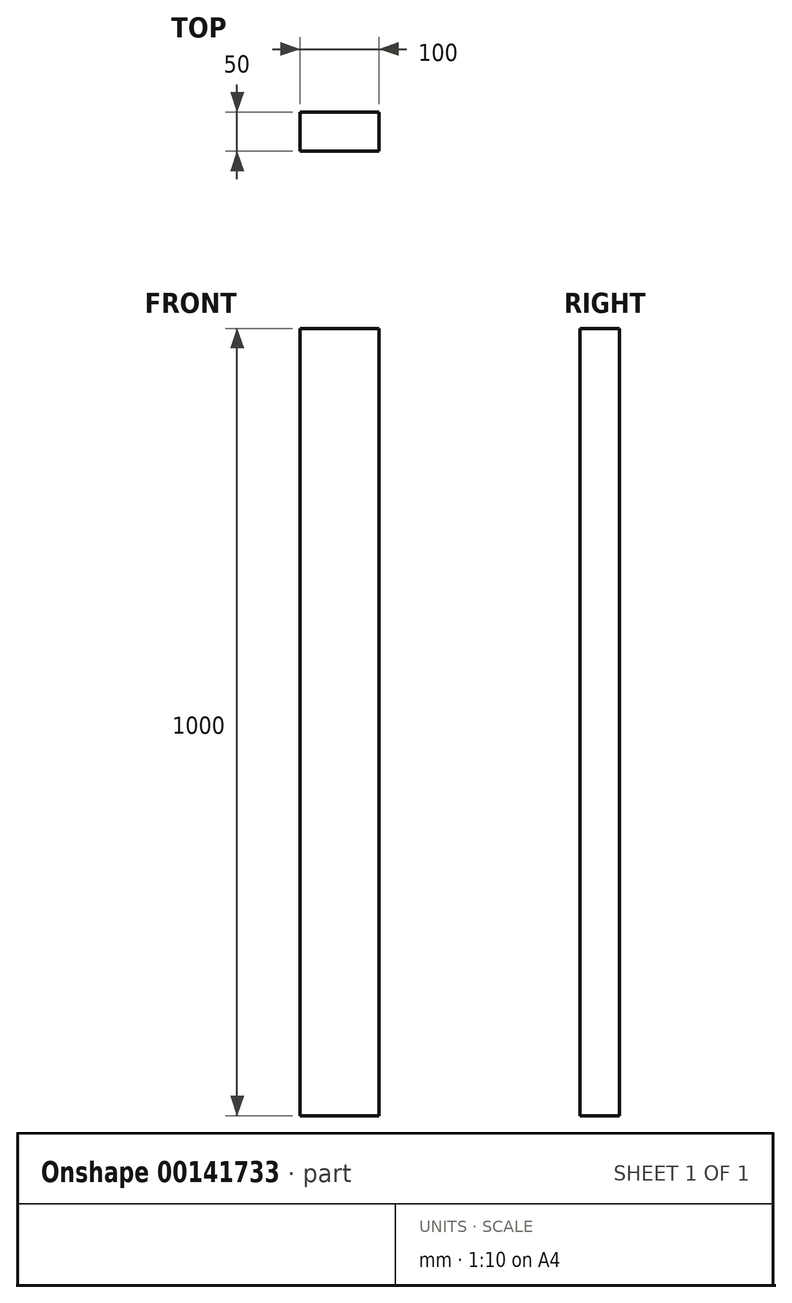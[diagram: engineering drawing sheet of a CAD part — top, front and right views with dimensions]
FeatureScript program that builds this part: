
annotation { "Feature Type Name" : "Feature", "Feature Type Description" : "" }
export const myFeature = defineFeature(function(context is Context, id is Id, definition is map)
    precondition{}
    {
        {
            var Q0;
            Q0=qCreatedBy(makeId("Top.planeOp"),FACE);
            var sketch = newSketch(context, id + "F0", { "sketchPlane" : qUnion([Q0])});
            skLineSegment(sketch, "E0.bottom", {"start": v(50, 25) * mm, "end": v(-50, 25) * mm});
            skLineSegment(sketch, "E0.top", {"start": v(50, -25) * mm, "end": v(-50, -25) * mm});
            skLineSegment(sketch, "E0.left", {"start": v(50, 25) * mm, "end": v(50, -25) * mm});
            skLineSegment(sketch, "E0.right", {"start": v(-50, 25) * mm, "end": v(-50, -25) * mm});
            skPoint(sketch, "E0.middle", {"position": v(0, 0) * mm});
            skSolve(sketch);
        }
        {
            var Q0;
            Q0=makeQuery(id+"F0.imprint","IMPRINT",FACE,{"disambiguationData":[TD([[makeQuery(id+"F0.imprint","IMPRINT",EDGE,{"derivedFrom":sQuery(id+"F0.wireOp",EDGE,"E0.bottom")}),1.0]])]});
            extrude(context, id + "F1", {"entities" : qUnion([Q0]), "depth" : 1000 * mm});
        }
    });
